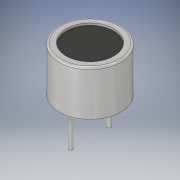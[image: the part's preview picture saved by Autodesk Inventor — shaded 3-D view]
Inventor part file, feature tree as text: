
AUTODESK INVENTOR PART (.ipt)
format: ipt  version: 2019 (Build 230136000, 136)  size: 164,352 bytes
history: native  units: mm
features: extrude x5, sketch x5, fillet x1
ambient origin geometry x8: Origin, YZ Plane, XZ Plane, XY Plane, X Axis, Y Axis, Z Axis, Center Point
bodies: Volumenkörper1 (feature_tree)
feature tree (11):
  extrude  "Extrusion1"  Depth=12.2mm TaperAngle=0.0deg
  fillet  "Rundung1"  Radius=0.5mm
  extrude  "Extrusion2"  Depth=0.5mm TaperAngle=0.0deg
  extrude  "Extrusion3"  Depth=10.0mm
  extrude  "Extrusion4"  Depth=1.0mm
  extrude  "Extrusion5"  Depth=10.0mm TaperAngle=0.0deg
  sketch  "Skizze1"  dims[d0=16.0mm d1=12.2mm d2=0.0mm d3=0.5mm]
  sketch  "Skizze2"  dims[d4=1.8mm d5=0.5mm d6=0.0mm]
  sketch  "Skizze3"  dims[d7=0.75mm d8=0.0mm d9=10.0mm]
  sketch  "Skizze4"  dims[d10=5.0mm d11=1.0mm]
  sketch  "Skizze5"  dims[d12=1.0mm d13=10.0mm d14=0.0mm d15=0.0mm d16=0.0mm d17=1.0mm d18=0.25mm d19=0.1mm d20=0.0mm]
